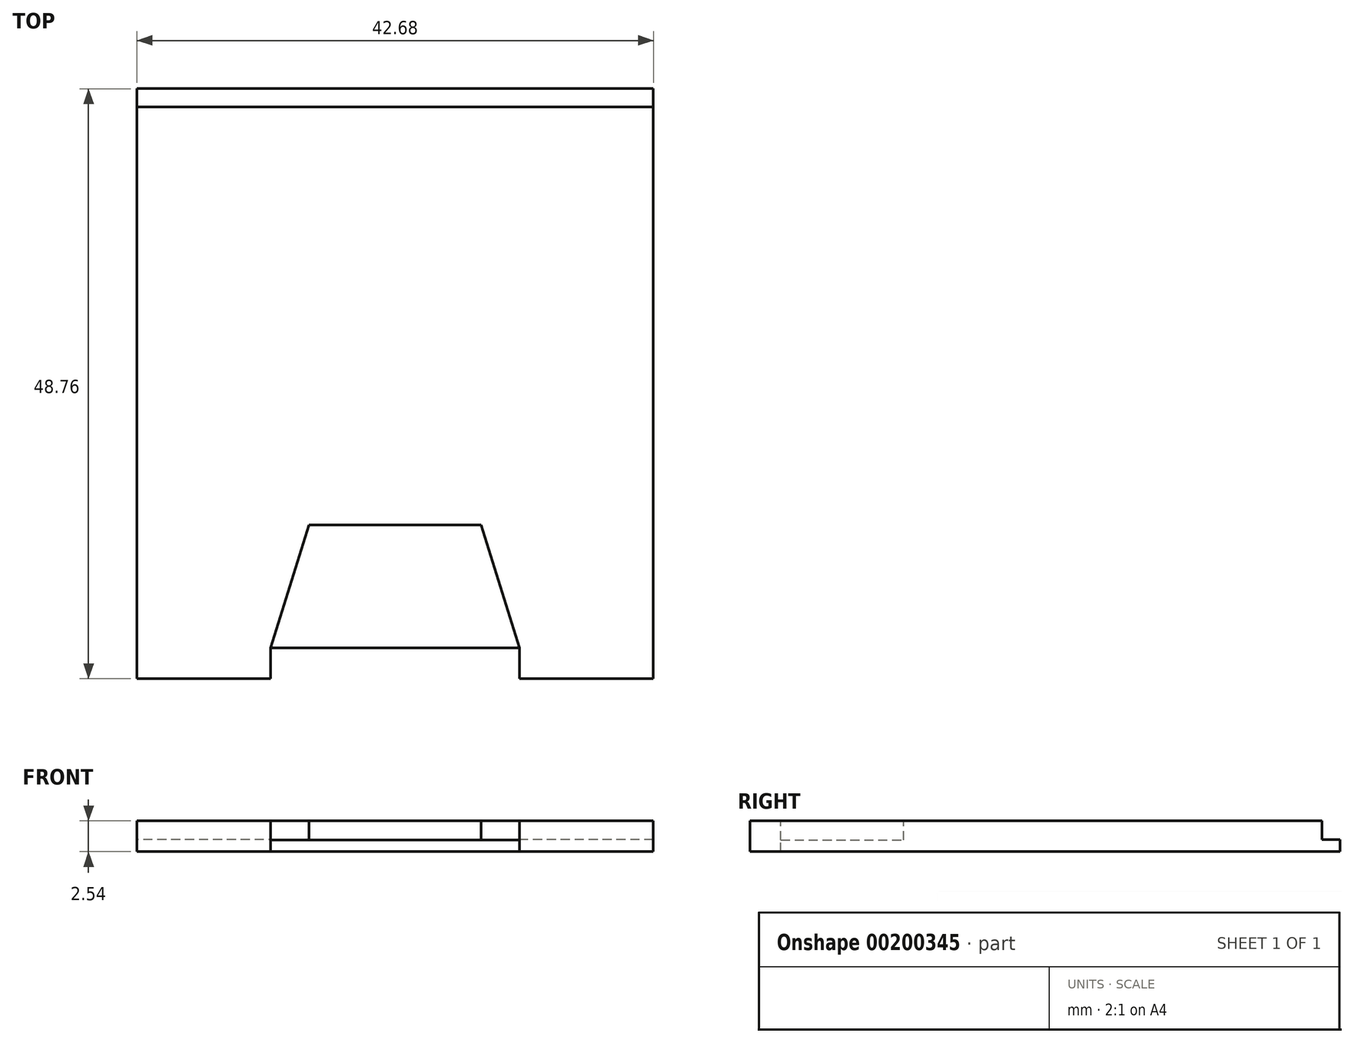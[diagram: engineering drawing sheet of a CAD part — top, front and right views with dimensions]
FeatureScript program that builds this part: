
annotation { "Feature Type Name" : "Feature", "Feature Type Description" : "" }
export const myFeature = defineFeature(function(context is Context, id is Id, definition is map)
    precondition{}
    {
        {
            var Q0;
            Q0=qCreatedBy(makeId("Top.planeOp"),FACE);
            var sketch = newSketch(context, id + "F0", { "sketchPlane" : qUnion([Q0])});
            skLineSegment(sketch, "E0.bottom", {"start": v(-21.34, 24.38) * mm, "end": v(21.34, 24.38) * mm});
            skLineSegment(sketch, "E0.top", {"start": v(-21.34, -24.38) * mm, "end": v(21.34, -24.38) * mm});
            skLineSegment(sketch, "E0.left", {"start": v(-21.34, 24.38) * mm, "end": v(-21.34, -24.38) * mm});
            skLineSegment(sketch, "E0.right", {"start": v(21.34, 24.38) * mm, "end": v(21.34, -24.38) * mm});
            skPoint(sketch, "E0.middle", {"position": v(0, 0) * mm});
            skSolve(sketch);
        }
        {
            var Q0;
            Q0 = qSketchRegion(id + "F0", true);
            extrude(context, id + "F1", {"entities" : qUnion([Q0]), "depth" : 2.54 * mm});
        }
        {
            var Q0;
            Q0=makeQuery(id+"F1.opExtrude","SWEPT_FACE",FACE,{"disambiguationData":[OSD([sQuery(id+"F0.wireOp",EDGE,"E0.bottom")])]});
            var sketch = newSketch(context, id + "F2", { "sketchPlane" : qUnion([Q0])});
            skLineSegment(sketch, "E1.bottom", {"start": v(-21.34, 2.54) * mm, "end": v(21.34, 2.54) * mm});
            skLineSegment(sketch, "E1.top", {"start": v(-21.34, 1) * mm, "end": v(21.34, 1) * mm});
            skLineSegment(sketch, "E1.left", {"start": v(-21.34, 2.54) * mm, "end": v(-21.34, 1) * mm});
            skLineSegment(sketch, "E1.right", {"start": v(21.34, 2.54) * mm, "end": v(21.34, 1) * mm});
            skSolve(sketch);
        }
        {
            var Q0;
            Q0 = qSketchRegion(id + "F2", true);
            extrude(context, id + "F3", {"entities" : qUnion([Q0]), "operationType" : NewBodyOperationType.REMOVE, "oppositeDirection" : true, "depth" : 1.5 * mm});
        }
        {
            var Q0;
            Q0=makeQuery(id+"F1.opExtrude","CAP_FACE",FACE,{"disambiguationData":[OSD([sQuery(id+"F0.wireOp",EDGE,"E0.bottom"),sQuery(id+"F0.wireOp",EDGE,"E0.top"),sQuery(id+"F0.wireOp",EDGE,"E0.left"),sQuery(id+"F0.wireOp",EDGE,"E0.right")])],"isStart":false});
            var sketch = newSketch(context, id + "F4", { "sketchPlane" : qUnion([Q0])});
            skLineSegment(sketch, "E2.bottom", {"start": v(-10.29, -24.38) * mm, "end": v(10.29, -24.38) * mm});
            skLineSegment(sketch, "E2.top", {"start": v(-10.29, -21.84) * mm, "end": v(10.29, -21.84) * mm});
            skLineSegment(sketch, "E2.left", {"start": v(-10.29, -24.38) * mm, "end": v(-10.29, -21.84) * mm});
            skLineSegment(sketch, "E2.right", {"start": v(10.29, -24.38) * mm, "end": v(10.29, -21.84) * mm});
            skPoint(sketch, "E3.endSnap0", {"position": v(0, -24.38) * mm});
            skSolve(sketch);
        }
        {
            var Q0;
            Q0 = qSketchRegion(id + "F4", true);
            extrude(context, id + "F5", {"entities" : qUnion([Q0]), "operationType" : NewBodyOperationType.REMOVE, "oppositeDirection" : true, "depth" : 5.08 * mm});
        }
        {
            var Q0;
            Q0=makeQuery(id+"F1.opExtrude","CAP_FACE",FACE,{"disambiguationData":[OSD([sQuery(id+"F0.wireOp",EDGE,"E0.bottom"),sQuery(id+"F0.wireOp",EDGE,"E0.top"),sQuery(id+"F0.wireOp",EDGE,"E0.left"),sQuery(id+"F0.wireOp",EDGE,"E0.right")])],"isStart":false});
            var sketch = newSketch(context, id + "F6", { "sketchPlane" : qUnion([Q0])});
            skLineSegment(sketch, "E4.bottom", {"start": v(-10.29, -21.84) * mm, "end": v(10.29, -21.84) * mm});
            skLineSegment(sketch, "E4.top", {"start": v(-7.11, -11.68) * mm, "end": v(7.11, -11.68) * mm});
            skLineSegment(sketch, "E5", {"start": v(-10.29, -21.84) * mm, "end": v(-7.11, -11.68) * mm});
            skLineSegment(sketch, "E6", {"start": v(10.29, -21.84) * mm, "end": v(7.11, -11.68) * mm});
            skPoint(sketch, "E7.orphan", {"position": v(-10.29, -11.68) * mm});
            skPoint(sketch, "E4.right.end.orphan", {"position": v(10.29, -11.68) * mm});
            skSolve(sketch);
        }
        {
            var Q0;
            Q0 = qSketchRegion(id + "F6", true);
            extrude(context, id + "F7", {"entities" : qUnion([Q0]), "operationType" : NewBodyOperationType.REMOVE, "oppositeDirection" : true, "depth" : 1.59 * mm});
        }
    });
